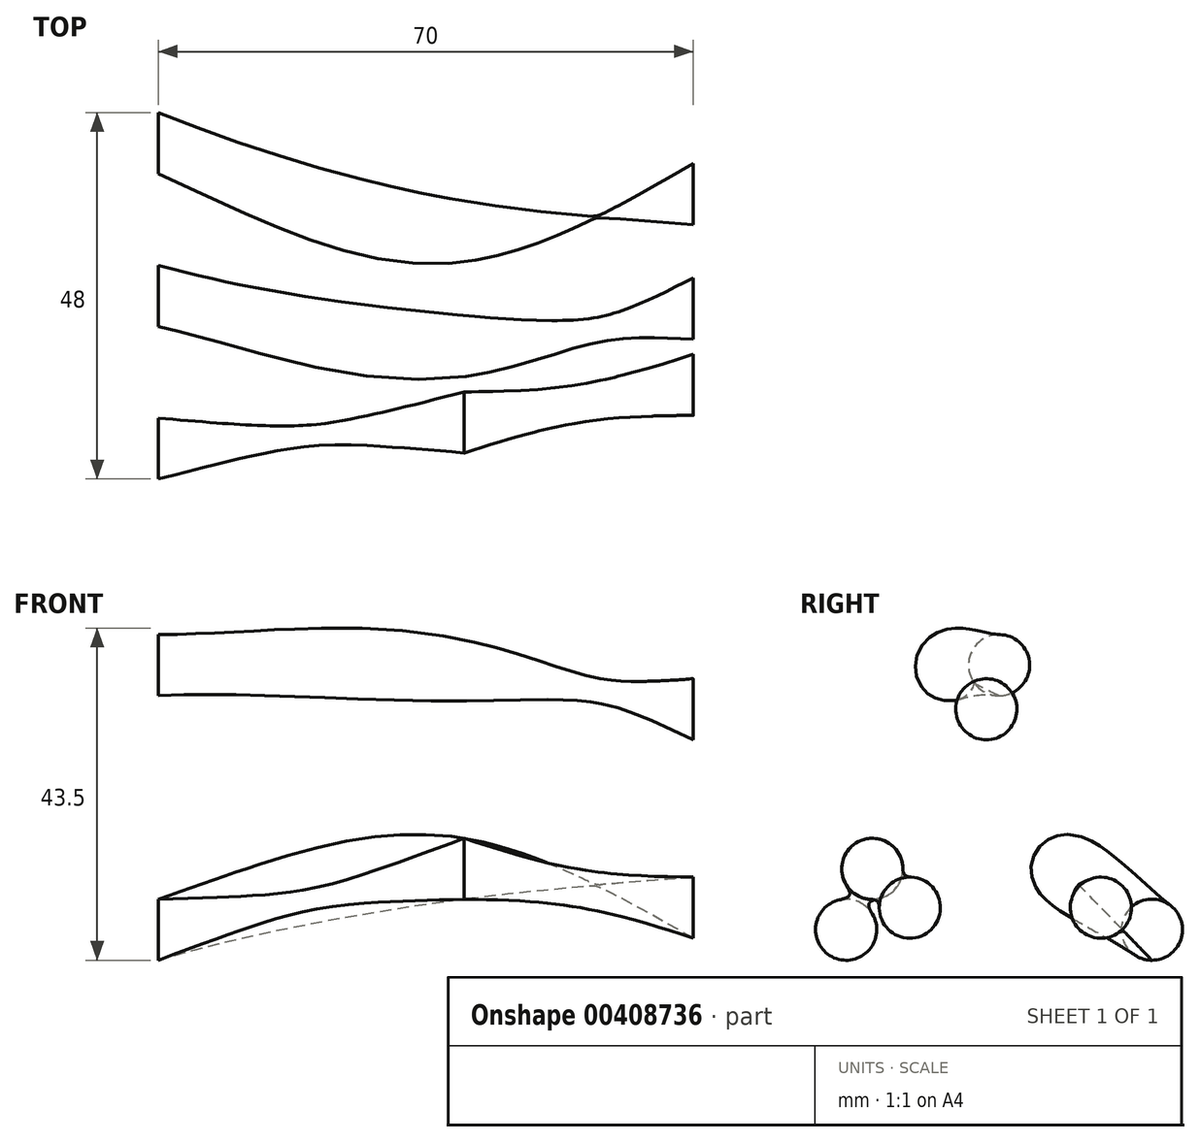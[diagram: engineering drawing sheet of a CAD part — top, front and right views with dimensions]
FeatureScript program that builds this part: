
annotation { "Feature Type Name" : "Feature", "Feature Type Description" : "" }
export const myFeature = defineFeature(function(context is Context, id is Id, definition is map)
    precondition{}
    {
        {
            var Q0;
            Q0=qCreatedBy(makeId("Right.planeOp"),FACE);
            var sketch = newSketch(context, id + "F0", { "sketchPlane" : qUnion([Q0])});
            skLineSegment(sketch, "E0", {"start": v(-20, -11.54) * mm, "end": v(0, 23.1) * mm, "construction": true});
            skLineSegment(sketch, "E1", {"start": v(0, 23.1) * mm, "end": v(20, -11.54) * mm, "construction": true});
            skLineSegment(sketch, "E2", {"start": v(20, -11.54) * mm, "end": v(-20, -11.54) * mm, "construction": true});
            skCircle(sketch, "E3", {"center": v(0, 23.1) * mm, "radius": 4 * mm});
            skCircle(sketch, "E4", {"center": v(-20, -11.54) * mm, "radius": 4 * mm});
            skCircle(sketch, "E5", {"center": v(20, -11.54) * mm, "radius": 4 * mm});
            skSolve(sketch);
        }
        {
            var Q0;
            Q0=qCreatedBy(makeId("Right.planeOp"),FACE);
            cPlane(context, id + "F1", {"entities" : qUnion([Q0]), "cplaneType" : CPlaneType.OFFSET, "offset" : 40 * mm, "width" : 150 * mm, "height" : 150 * mm});
        }
        {
            var Q0;
            Q0=qCreatedBy(id+"F1.planeOp",FACE);
            var sketch = newSketch(context, id + "F2", { "sketchPlane" : qUnion([Q0])});
            skLineSegment(sketch, "E6", {"start": v(-16.58, -3.57) * mm, "end": v(-6.58, 22.4) * mm, "construction": true});
            skLineSegment(sketch, "E7", {"start": v(-6.58, 22.4) * mm, "end": v(8.42, -3.57) * mm, "construction": true});
            skLineSegment(sketch, "E8", {"start": v(8.42, -3.57) * mm, "end": v(-16.58, -3.57) * mm, "construction": true});
            skCircle(sketch, "E9", {"center": v(-6.58, 22.4) * mm, "radius": 4 * mm});
            skCircle(sketch, "E10", {"center": v(-16.58, -3.57) * mm, "radius": 4 * mm});
            skCircle(sketch, "E11", {"center": v(8.42, -3.57) * mm, "radius": 4 * mm});
            skSolve(sketch);
        }
        {
            var Q0;
            Q0=qCreatedBy(id+"F1.planeOp",FACE);
            cPlane(context, id + "F3", {"entities" : qUnion([Q0]), "cplaneType" : CPlaneType.OFFSET, "offset" : 30 * mm, "width" : 150 * mm, "height" : 150 * mm});
        }
        {
            var Q0;
            Q0=qCreatedBy(id+"F3.planeOp",FACE);
            var sketch = newSketch(context, id + "F4", { "sketchPlane" : qUnion([Q0])});
            skLineSegment(sketch, "E12", {"start": v(-11.67, -8.66) * mm, "end": v(-1.67, 17.32) * mm, "construction": true});
            skLineSegment(sketch, "E13", {"start": v(-1.67, 17.32) * mm, "end": v(13.33, -8.66) * mm, "construction": true});
            skLineSegment(sketch, "E14", {"start": v(13.33, -8.66) * mm, "end": v(-11.67, -8.66) * mm, "construction": true});
            skCircle(sketch, "E15", {"center": v(-1.67, 17.32) * mm, "radius": 4 * mm});
            skCircle(sketch, "E16", {"center": v(-11.67, -8.66) * mm, "radius": 4 * mm});
            skCircle(sketch, "E17", {"center": v(13.33, -8.66) * mm, "radius": 4 * mm});
            skSolve(sketch);
        }
        {
            var Q0;
            Q0=makeQuery(id+"F0.imprint","IMPRINT",FACE,{"disambiguationData":[TD([[makeQuery(id+"F0.imprint","IMPRINT",EDGE,{"derivedFrom":sQuery(id+"F0.wireOp",EDGE,"E3")}),1.0]])]});
            var Q1;
            Q1=makeQuery(id+"F2.imprint","IMPRINT",FACE,{"disambiguationData":[TD([[makeQuery(id+"F2.imprint","IMPRINT",EDGE,{"derivedFrom":sQuery(id+"F2.wireOp",EDGE,"E9")}),1.0]])]});
            var Q2;
            Q2=makeQuery(id+"F4.imprint","IMPRINT",FACE,{"disambiguationData":[TD([[makeQuery(id+"F4.imprint","IMPRINT",EDGE,{"derivedFrom":sQuery(id+"F4.wireOp",EDGE,"E15")}),1.0]])]});
            loft(context, id + "F5", {"sheetProfilesArray" : [{ "sheetProfileEntities" : qUnion([Q0]) }, { "sheetProfileEntities" : qUnion([Q1]) }, { "sheetProfileEntities" : qUnion([Q2]) }]});
        }
        {
            var Q0;
            Q0=makeQuery(id+"F0.imprint","IMPRINT",FACE,{"disambiguationData":[TD([[makeQuery(id+"F0.imprint","IMPRINT",EDGE,{"derivedFrom":sQuery(id+"F0.wireOp",EDGE,"E5")}),1.0]])]});
            var Q1;
            Q1=makeQuery(id+"F2.imprint","IMPRINT",FACE,{"disambiguationData":[TD([[makeQuery(id+"F2.imprint","IMPRINT",EDGE,{"derivedFrom":sQuery(id+"F2.wireOp",EDGE,"E11")}),1.0]])]});
            var Q2;
            Q2=makeQuery(id+"F4.imprint","IMPRINT",FACE,{"disambiguationData":[TD([[makeQuery(id+"F4.imprint","IMPRINT",EDGE,{"derivedFrom":sQuery(id+"F4.wireOp",EDGE,"E17")}),1.0]])]});
            loft(context, id + "F6", {"sheetProfilesArray" : [{ "sheetProfileEntities" : qUnion([Q0]) }, { "sheetProfileEntities" : qUnion([Q1]) }, { "sheetProfileEntities" : qUnion([Q2]) }]});
        }
        {
            var Q0;
            Q0=makeQuery(id+"F2.imprint","IMPRINT",FACE,{"disambiguationData":[TD([[makeQuery(id+"F2.imprint","IMPRINT",EDGE,{"derivedFrom":sQuery(id+"F2.wireOp",EDGE,"E10")}),1.0]])]});
            var Q1;
            Q1=makeQuery(id+"F0.imprint","IMPRINT",FACE,{"disambiguationData":[TD([[makeQuery(id+"F0.imprint","IMPRINT",EDGE,{"derivedFrom":sQuery(id+"F0.wireOp",EDGE,"E4")}),1.0]])]});
            loft(context, id + "F7", {"sheetProfilesArray" : [{ "sheetProfileEntities" : qUnion([Q0]) }, { "sheetProfileEntities" : qUnion([Q1]) }]});
        }
        {
            var Q0;
            Q0=makeQuery(id+"F2.imprint","IMPRINT",FACE,{"disambiguationData":[TD([[makeQuery(id+"F2.imprint","IMPRINT",EDGE,{"derivedFrom":sQuery(id+"F2.wireOp",EDGE,"E10")}),1.0]])]});
            var Q1;
            Q1=makeQuery(id+"F4.imprint","IMPRINT",FACE,{"disambiguationData":[TD([[makeQuery(id+"F4.imprint","IMPRINT",EDGE,{"derivedFrom":sQuery(id+"F4.wireOp",EDGE,"E16")}),1.0]])]});
            loft(context, id + "F8", {"sheetProfilesArray" : [{ "sheetProfileEntities" : qUnion([Q0]) }, { "sheetProfileEntities" : qUnion([Q1]) }]});
        }
    });
